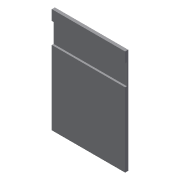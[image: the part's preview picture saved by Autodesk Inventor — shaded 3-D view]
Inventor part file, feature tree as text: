
AUTODESK INVENTOR PART (.ipt)
format: ipt  version: 2019 (Build 230136000, 136)  size: 176,128 bytes
history: native  units: mm
features: extrude x3, sketch x3, projected_geometry x2, pattern_linear x1
ambient origin geometry x8: Origin, YZ Plane, XZ Plane, XY Plane, X Axis, Y Axis, Z Axis, Center Point
bodies: Solid1 (feature_tree)
feature tree (9):
  extrude  "Extrusion1"  Depth=27.0mm
  extrude  "Extrusion2"  Depth=6.75mm
  extrude  "Extrusion3"  Depth=0.6mm TaperAngle=0.0deg
  pattern_linear  "Rectangular Pattern1"  Spacing1=3.4mm  [1 undecoded]
  sketch  "Sketch1"  dims[d0=23.76mm d1=27.0mm]
  sketch  "Sketch2"  dims[d2=1.0mm d3=0.0mm d4=6.75mm]
  projected_geometry  "Projected Loop1"
  sketch  "Sketch3"  dims[d5=3.3mm d6=0.6mm d7=0.0mm d9=3.4mm d10=5.25mm d11=0.6mm d12=0.0mm d13=240.0mm d15=0.27mm]
  projected_geometry  "Projected Loop2"
note: 1 required parameter value undecoded (feature->parameter linkage not recoverable at this tier; creation-order binding heuristic only, values carry confidence <= 0.55)
